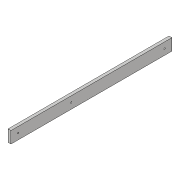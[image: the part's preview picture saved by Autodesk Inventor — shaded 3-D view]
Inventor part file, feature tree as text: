
AUTODESK INVENTOR PART (.ipt)
format: ipt  version: 2018.3 (Build 223284000, 284)  size: 87,552 bytes
history: native  units: in
note: dims shown in document units (in); Inventor stores cm internally (conversion verified against a paired STEP export)
features: extrude x2, sketch x2
ambient origin geometry x8: Origin, YZ Plane, XZ Plane, XY Plane, X Axis, Y Axis, Z Axis, Center Point
bodies: Solid1 (feature_tree)
feature tree (4):
  extrude  "Extrusion1"  Depth=0.125in
  extrude  "Extrusion2"  Depth=6.895in
  sketch  "Sketch1"  dims[d0=0.5in d1=0.125in]
  sketch  "Sketch2"  dims[d2=6.895in d3=0.0in d4=0.0625in d5=0.3125in d6=1.0in d7=0.0in d8=4.0in d9=2.27in d10=0.0625in d11=0.0625in]
